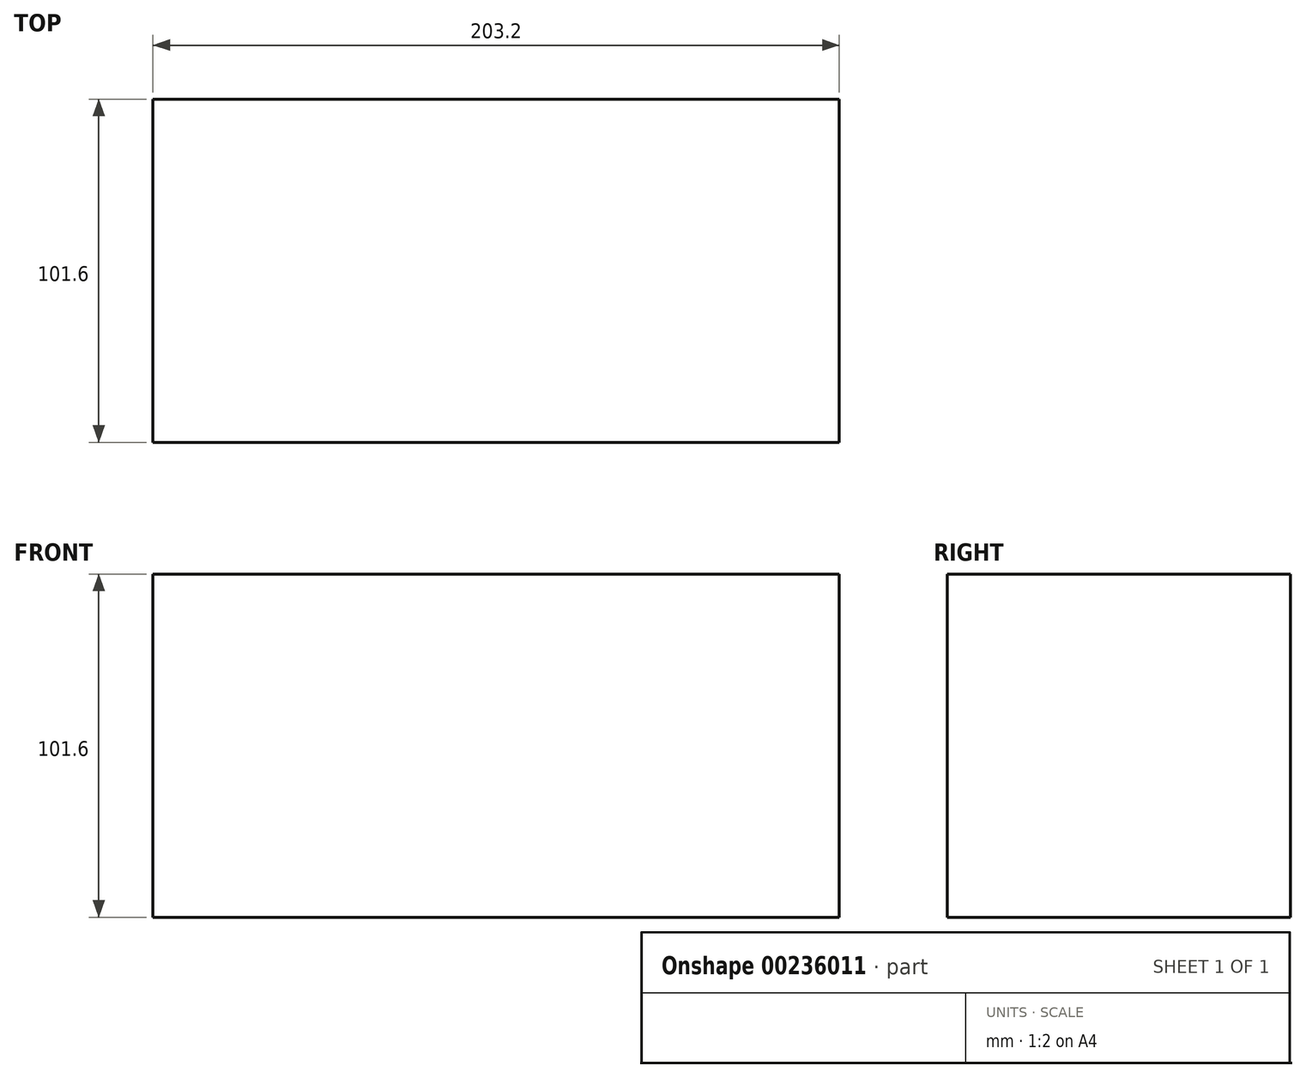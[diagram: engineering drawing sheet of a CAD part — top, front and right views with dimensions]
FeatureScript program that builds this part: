
annotation { "Feature Type Name" : "Feature", "Feature Type Description" : "" }
export const myFeature = defineFeature(function(context is Context, id is Id, definition is map)
    precondition{}
    {
        {
            var Q0;
            Q0=qCreatedBy(makeId("Top.planeOp"),FACE);
            var sketch = newSketch(context, id + "F0", { "sketchPlane" : qUnion([Q0])});
            skLineSegment(sketch, "E0.bottom", {"start": v(-131.93, -34.84) * mm, "end": v(71.27, -34.84) * mm});
            skLineSegment(sketch, "E0.top", {"start": v(-131.93, 66.76) * mm, "end": v(71.27, 66.76) * mm});
            skLineSegment(sketch, "E0.left", {"start": v(-131.93, -34.84) * mm, "end": v(-131.93, 66.76) * mm});
            skLineSegment(sketch, "E0.right", {"start": v(71.27, -34.84) * mm, "end": v(71.27, 66.76) * mm});
            skSolve(sketch);
        }
        {
            var Q0;
            Q0=makeQuery(id+"F0.imprint","IMPRINT",FACE,{"disambiguationData":[TD([[makeQuery(id+"F0.imprint","IMPRINT",EDGE,{"derivedFrom":sQuery(id+"F0.wireOp",EDGE,"E0.bottom")}),1.0]])]});
            extrude(context, id + "F1", {"entities" : qUnion([Q0]), "depth" : 101.6 * mm});
        }
    });
